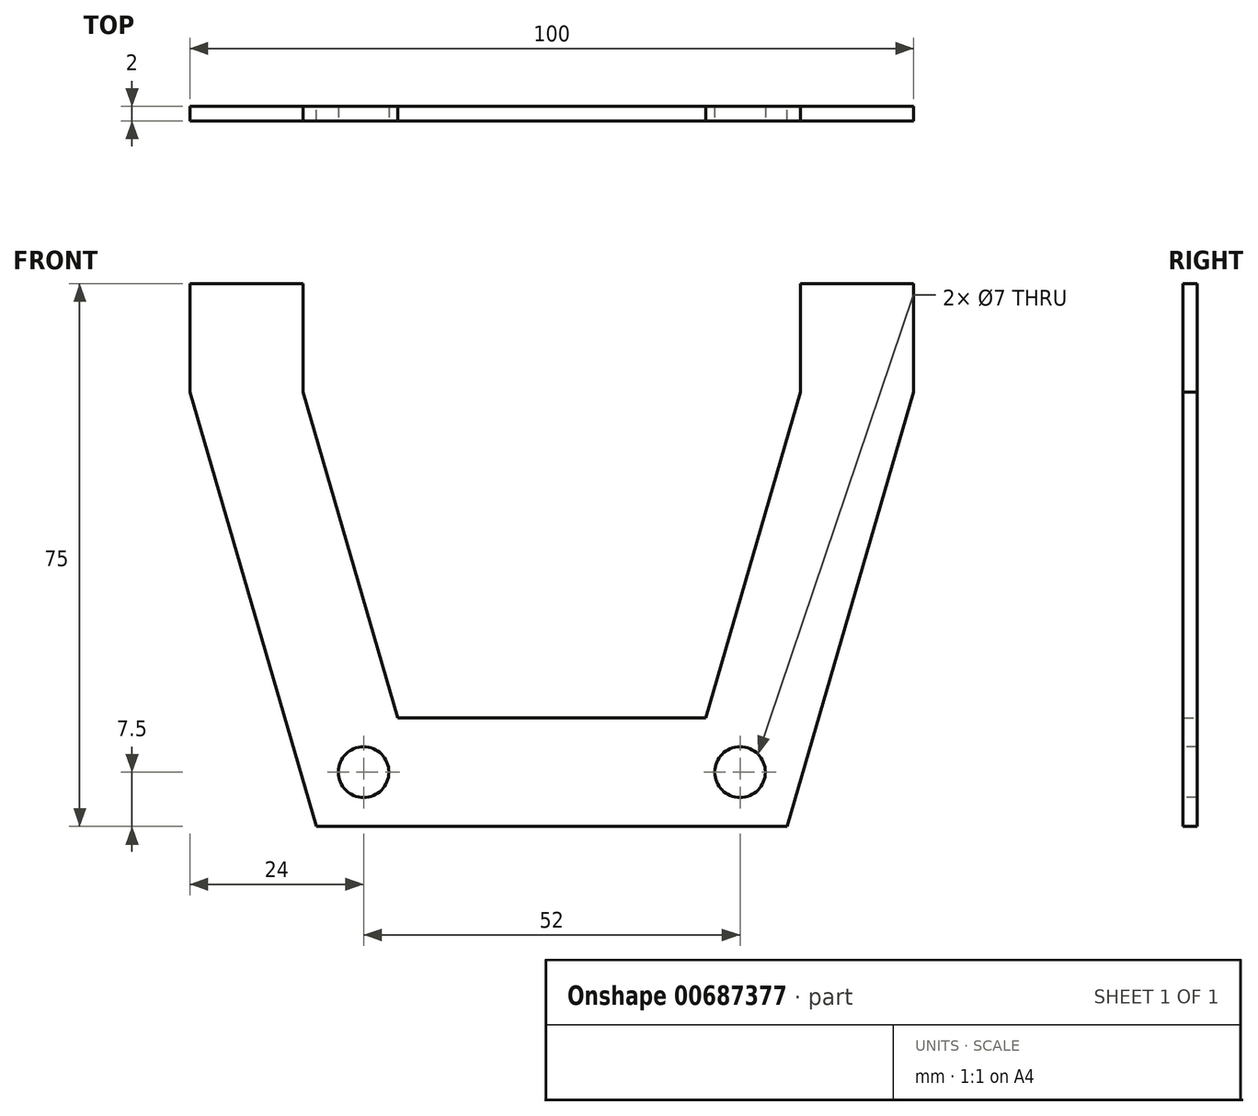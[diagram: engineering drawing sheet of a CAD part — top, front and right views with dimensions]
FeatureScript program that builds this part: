
annotation { "Feature Type Name" : "Feature", "Feature Type Description" : "" }
export const myFeature = defineFeature(function(context is Context, id is Id, definition is map)
    precondition{}
    {
        {
            var Q0;
            Q0=qCreatedBy(makeId("Front.planeOp"),FACE);
            var sketch = newSketch(context, id + "F0", { "sketchPlane" : qUnion([Q0])});
            skLineSegment(sketch, "E0.bottom", {"start": v(-32.5, -37.5) * mm, "end": v(32.5, -37.5) * mm});
            skLineSegment(sketch, "E0.top", {"start": v(-50, 37.5) * mm, "end": v(-34.37, 37.5) * mm});
            skLineSegment(sketch, "E0.left", {"start": v(-50, 22.5) * mm, "end": v(-50, 37.5) * mm});
            skLineSegment(sketch, "E0.right", {"start": v(50, 22.5) * mm, "end": v(50, 37.5) * mm});
            skLineSegment(sketch, "E1", {"start": v(32.5, -37.5) * mm, "end": v(50, 22.5) * mm});
            skLineSegment(sketch, "E2", {"start": v(-32.5, -37.5) * mm, "end": v(-50, 22.5) * mm});
            skPoint(sketch, "E3.orphan", {"position": v(50, -37.5) * mm});
            skPoint(sketch, "E4.orphan", {"position": v(-50, -37.5) * mm});
            skLineSegment(sketch, "E5.2", {"start": v(21.25, -22.5) * mm, "end": v(34.38, 22.5) * mm});
            skLineSegment(sketch, "E5.4", {"start": v(-21.25, -22.5) * mm, "end": v(21.25, -22.5) * mm});
            skLineSegment(sketch, "E5.5", {"start": v(-21.25, -22.5) * mm, "end": v(-34.37, 22.5) * mm});
            skLineSegment(sketch, "E6", {"start": v(-34.37, 22.5) * mm, "end": v(-34.37, 37.5) * mm});
            skLineSegment(sketch, "E7", {"start": v(34.38, 22.5) * mm, "end": v(34.38, 37.5) * mm});
            skLineSegment(sketch, "E8.trimOffspring", {"start": v(34.38, 37.5) * mm, "end": v(50, 37.5) * mm});
            skSolve(sketch);
        }
        {
            var Q0;
            Q0=makeQuery(id+"F0.imprint","IMPRINT",FACE,{"disambiguationData":[TD([[makeQuery(id+"F0.imprint","IMPRINT",EDGE,{"derivedFrom":sQuery(id+"F0.wireOp",EDGE,"E0.bottom")}),1.0]])]});
            extrude(context, id + "F1", {"entities" : qUnion([Q0]), "depth" : 2 * mm, "offsetDistance" : 25 * mm});
        }
        {
            var Q0;
            Q0=makeQuery(id+"F1.opExtrude","CAP_FACE",FACE,{"disambiguationData":[OSD([sQuery(id+"F0.wireOp",EDGE,"E0.bottom"),sQuery(id+"F0.wireOp",EDGE,"E0.top"),sQuery(id+"F0.wireOp",EDGE,"E0.left"),sQuery(id+"F0.wireOp",EDGE,"E0.right"),sQuery(id+"F0.wireOp",EDGE,"E1"),sQuery(id+"F0.wireOp",EDGE,"E2"),sQuery(id+"F0.wireOp",EDGE,"E5.2"),sQuery(id+"F0.wireOp",EDGE,"E5.4"),sQuery(id+"F0.wireOp",EDGE,"E5.5"),sQuery(id+"F0.wireOp",EDGE,"E6"),sQuery(id+"F0.wireOp",EDGE,"E7"),sQuery(id+"F0.wireOp",EDGE,"E8.trimOffspring")])],"isStart":false});
            var sketch = newSketch(context, id + "F2", { "sketchPlane" : qUnion([Q0])});
            skPoint(sketch, "E9", {"position": v(-26, -30) * mm});
            skPoint(sketch, "E10", {"position": v(26, -30) * mm});
            skLineSegment(sketch, "E11", {"start": v(0, 0) * mm, "end": v(0, -37.5) * mm, "construction": true});
            skPoint(sketch, "E12", {"position": v(-42.5, 30) * mm});
            skPoint(sketch, "E13", {"position": v(41.88, 30) * mm});
            skSolve(sketch);
        }
        {
            var Q0;
            Q0=sQuery(id+"F2.wireOp",VERTEX,"E9");
            var Q1;
            Q1=sQuery(id+"F2.wireOp",VERTEX,"E10");
            var Q2;
            Q2=makeQuery(id+"F1.opExtrude","SWEPT_BODY",BODY,{"disambiguationData":[OSD([sQuery(id+"F0.wireOp",EDGE,"E0.bottom"),sQuery(id+"F0.wireOp",EDGE,"E0.top"),sQuery(id+"F0.wireOp",EDGE,"E0.left"),sQuery(id+"F0.wireOp",EDGE,"E0.right"),sQuery(id+"F0.wireOp",EDGE,"E1"),sQuery(id+"F0.wireOp",EDGE,"E2"),sQuery(id+"F0.wireOp",EDGE,"E5.2"),sQuery(id+"F0.wireOp",EDGE,"E5.4"),sQuery(id+"F0.wireOp",EDGE,"E5.5"),sQuery(id+"F0.wireOp",EDGE,"E6"),sQuery(id+"F0.wireOp",EDGE,"E7"),sQuery(id+"F0.wireOp",EDGE,"E8.trimOffspring")])]});
            hole(context, id + "F3", {"style" : HoleStyle.SIMPLE, "endStyle" : HoleEndStyle.THROUGH, "holeDiameter" : 7 * mm, "majorDiameter" : 5 * mm, "isTappedThrough" : true, "tappedDepth" : 12 * mm, "tapClearance" : 3, "locations" : qUnion([Q0, Q1]), "scope" : qUnion([Q2])});
        }
    });
